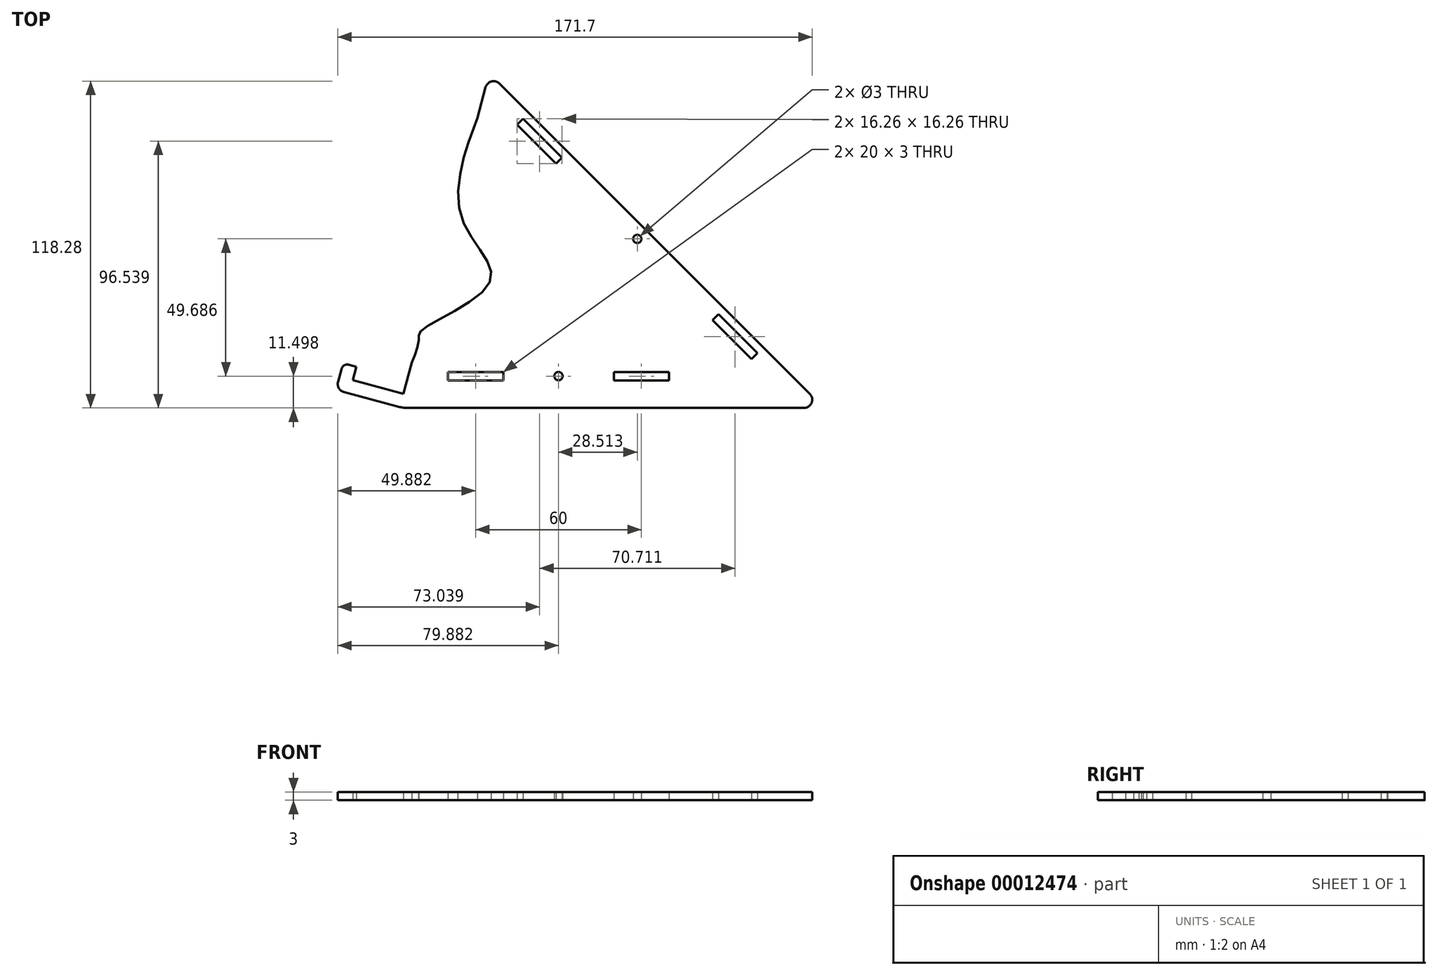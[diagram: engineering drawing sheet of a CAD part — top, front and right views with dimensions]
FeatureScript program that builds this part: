
annotation { "Feature Type Name" : "Feature", "Feature Type Description" : "" }
export const myFeature = defineFeature(function(context is Context, id is Id, definition is map)
    precondition{}
    {
        {
            var Q0;
            Q0=qCreatedBy(makeId("Top.planeOp"),FACE);
            var sketch = newSketch(context, id + "F0", { "sketchPlane" : qUnion([Q0])});
            skLineSegment(sketch, "E0", {"start": v(-70.63, -27.13) * mm, "end": v(-69.36, -22.42) * mm});
            skLineSegment(sketch, "E1", {"start": v(-66.76, -20.92) * mm, "end": v(-63.98, -21.66) * mm});
            skLineSegment(sketch, "E2", {"start": v(-63.98, -21.66) * mm, "end": v(-65.28, -26.5) * mm});
            skLineSegment(sketch, "E3", {"start": v(-65.28, -26.5) * mm, "end": v(-46.93, -31.41) * mm});
            skLineSegment(sketch, "E4", {"start": v(-46.93, -31.41) * mm, "end": v(-43.92, -20.2) * mm});
            skLineSegment(sketch, "E5", {"start": v(-12.2, 80.83) * mm, "end": v(100.1, -31.46) * mm});
            skLineSegment(sketch, "E6", {"start": v(97.97, -36.58) * mm, "end": v(-45.63, -36.58) * mm});
            skLineSegment(sketch, "E7", {"start": v(-48.22, -36.24) * mm, "end": v(-68.5, -30.8) * mm});
            skPoint(sketch, "E8.visualSharp", {"position": v(-46.95, -36.58) * mm});
            skArc(sketch, "E8.filletArc", {"start": v(-48.22, -36.24) * mm, "mid": v(-46.94, -36.5) * mm, "end": v(-45.63, -36.58) * mm});
            skPoint(sketch, "E9.visualSharp", {"position": v(-63.98, -21.66) * mm});
            skArc(sketch, "E10.filletArc", {"start": v(-66.76, -20.92) * mm, "mid": v(-68.37, -21.13) * mm, "end": v(-69.36, -22.42) * mm});
            skPoint(sketch, "E11.visualSharp", {"position": v(-71.4, -30.03) * mm});
            skArc(sketch, "E11.filletArc", {"start": v(-70.63, -27.13) * mm, "mid": v(-70.33, -29.4) * mm, "end": v(-68.5, -30.8) * mm});
            skPoint(sketch, "E12.visualSharp", {"position": v(-15.87, 84.5) * mm});
            skArc(sketch, "E12.filletArc", {"start": v(-12.2, 80.83) * mm, "mid": v(-15.1, 81.6) * mm, "end": v(-17.21, 79.48) * mm});
            skPoint(sketch, "E13.visualSharp", {"position": v(105.21, -36.58) * mm});
            skArc(sketch, "E13.filletArc", {"start": v(97.97, -36.58) * mm, "mid": v(100.74, -34.73) * mm, "end": v(100.1, -31.46) * mm});
            skLineSegment(sketch, "E14", {"start": v(-20.2, 68.31) * mm, "end": v(-17.21, 79.48) * mm});
            skFitSpline(sketch, "E15", {"points": [v(-43.92, -20.2) * mm, v(-41.32, -11.67) * mm, v(-40.62, -8.63) * mm, v(-15.58, 9.16) * mm, v(-26.34, 33.73) * mm, v(-20.2, 68.31) * mm], "startDerivative": vector(25.01, 63.29) * mm, "endDerivative": vector(25.25, 70.81) * mm});
            skLineSegment(sketch, "E16.bottom", {"start": v(-3.7, 68.1) * mm, "end": v(10.44, 53.95) * mm});
            skLineSegment(sketch, "E16.top", {"start": v(-5.82, 65.97) * mm, "end": v(8.32, 51.83) * mm});
            skLineSegment(sketch, "E16.left", {"start": v(-3.7, 68.1) * mm, "end": v(-5.82, 65.97) * mm});
            skLineSegment(sketch, "E16.right", {"start": v(10.44, 53.95) * mm, "end": v(8.32, 51.83) * mm});
            skLineSegment(sketch, "E17.bottom", {"start": v(67, -2.62) * mm, "end": v(81.15, -16.76) * mm});
            skLineSegment(sketch, "E17.top", {"start": v(64.89, -4.74) * mm, "end": v(79.03, -18.88) * mm});
            skLineSegment(sketch, "E17.left", {"start": v(67, -2.62) * mm, "end": v(64.89, -4.74) * mm});
            skLineSegment(sketch, "E17.right", {"start": v(81.15, -16.76) * mm, "end": v(79.03, -18.88) * mm});
            skCircle(sketch, "E18", {"center": v(37.66, 24.6) * mm, "radius": 1.5 * mm});
            skLineSegment(sketch, "E19.bottom", {"start": v(-30.85, -23.58) * mm, "end": v(-10.85, -23.58) * mm});
            skLineSegment(sketch, "E19.top", {"start": v(-30.85, -26.58) * mm, "end": v(-10.85, -26.58) * mm});
            skLineSegment(sketch, "E19.left", {"start": v(-30.85, -23.58) * mm, "end": v(-30.85, -26.58) * mm});
            skLineSegment(sketch, "E19.right", {"start": v(-10.85, -23.58) * mm, "end": v(-10.85, -26.58) * mm});
            skLineSegment(sketch, "E20.bottom", {"start": v(29.15, -23.58) * mm, "end": v(49.15, -23.58) * mm});
            skLineSegment(sketch, "E20.top", {"start": v(29.15, -26.58) * mm, "end": v(49.15, -26.58) * mm});
            skLineSegment(sketch, "E20.left", {"start": v(29.15, -23.58) * mm, "end": v(29.15, -26.58) * mm});
            skLineSegment(sketch, "E20.right", {"start": v(49.15, -23.58) * mm, "end": v(49.15, -26.58) * mm});
            skCircle(sketch, "E21", {"center": v(9.15, -25.08) * mm, "radius": 1.5 * mm});
            skSolve(sketch);
        }
        {
            var Q0;
            Q0 = qSketchRegion(id + "F0", true);
            extrude(context, id + "F1", {"entities" : qUnion([Q0]), "depth" : 3 * mm});
        }
    });
